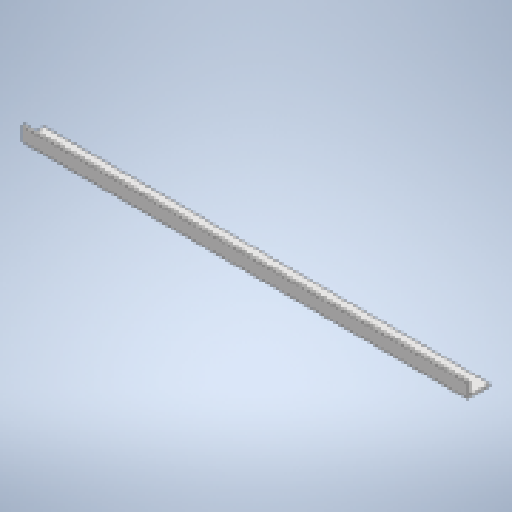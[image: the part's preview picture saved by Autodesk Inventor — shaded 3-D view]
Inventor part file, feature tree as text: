
AUTODESK INVENTOR PART (.ipt)
format: ipt  version: 2023 (Build 270158000, 158)  size: 139,776 bytes
history: native  units: in
note: dims shown in document units (in); Inventor stores cm internally (conversion verified against a paired STEP export)
features: extrude x1, sketch x1
ambient origin geometry x8: Origin, YZ Plane, XZ Plane, XY Plane, X Axis, Y Axis, Z Axis, Center Point
bodies: Solid1 (feature_tree)
feature tree (2):
  extrude  "Extrusion1"  Depth=2.3333in
  sketch  "Sketch1"  dims[d0=1.5in d1=2.3333in d2=0.25in d3=0.25in d4=47.2441in d5=0.0in]
